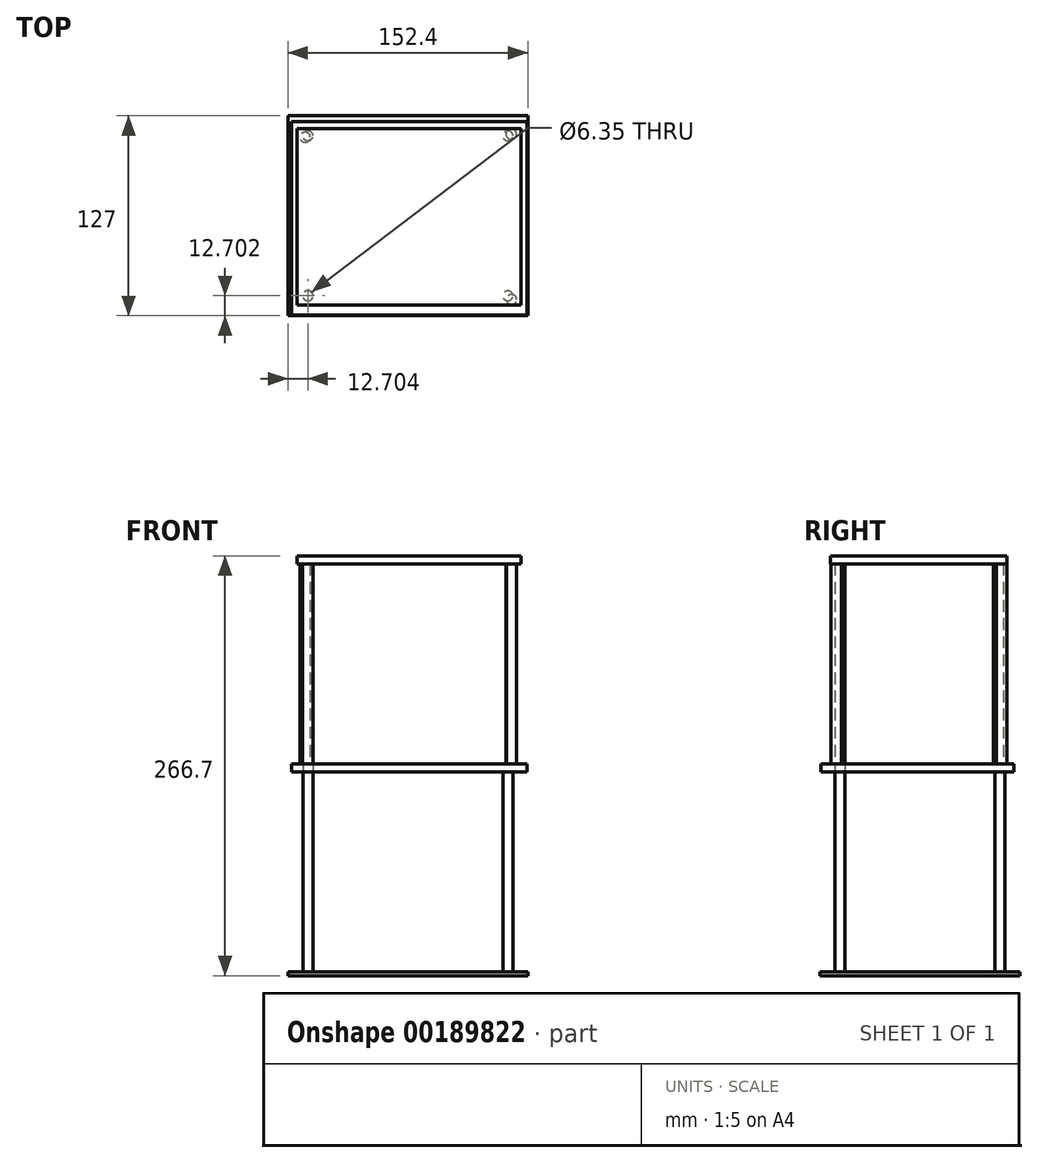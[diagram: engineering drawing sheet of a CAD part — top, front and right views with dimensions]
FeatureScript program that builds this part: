
annotation { "Feature Type Name" : "Feature", "Feature Type Description" : "" }
export const myFeature = defineFeature(function(context is Context, id is Id, definition is map)
    precondition{}
    {
        {
            var Q0;
            Q0=qCreatedBy(makeId("Top.planeOp"),FACE);
            var sketch = newSketch(context, id + "F0", { "sketchPlane" : qUnion([Q0])});
            skLineSegment(sketch, "E0.bottom", {"start": v(-67.97, -61.32) * mm, "end": v(84.43, -61.32) * mm});
            skLineSegment(sketch, "E0.top", {"start": v(-67.97, 65.68) * mm, "end": v(84.43, 65.68) * mm});
            skLineSegment(sketch, "E0.left", {"start": v(-67.97, -61.32) * mm, "end": v(-67.97, 65.68) * mm});
            skLineSegment(sketch, "E0.right", {"start": v(84.43, -61.32) * mm, "end": v(84.43, 65.68) * mm});
            skSolve(sketch);
        }
        {
            var Q0;
            Q0 = qSketchRegion(id + "F0", true);
            extrude(context, id + "F1", {"entities" : qUnion([Q0]), "oppositeDirection" : true, "depth" : 2.54 * mm});
        }
        {
            var Q0;
            Q0=makeQuery(id+"F1.opExtrude","CAP_FACE",FACE,{"disambiguationData":[OSD([sQuery(id+"F0.wireOp",EDGE,"E0.bottom"),sQuery(id+"F0.wireOp",EDGE,"E0.top"),sQuery(id+"F0.wireOp",EDGE,"E0.left"),sQuery(id+"F0.wireOp",EDGE,"E0.right")])],"isStart":true});
            var sketch = newSketch(context, id + "F2", { "sketchPlane" : qUnion([Q0])});
            skCircle(sketch, "E1", {"center": v(-55.27, -48.62) * mm, "radius": 3.18 * mm});
            skCircle(sketch, "E2", {"center": v(-55.27, 52.98) * mm, "radius": 3.18 * mm});
            skCircle(sketch, "E3", {"center": v(71.73, 52.98) * mm, "radius": 3.18 * mm});
            skCircle(sketch, "E4", {"center": v(71.73, -48.62) * mm, "radius": 3.18 * mm});
            skSolve(sketch);
        }
        {
            var Q0;
            Q0 = qSketchRegion(id + "F2", true);
            extrude(context, id + "F3", {"entities" : qUnion([Q0]), "operationType" : NewBodyOperationType.ADD, "depth" : 127 * mm});
        }
        {
            var Q0;
            Q0=makeQuery(id+"F3.opExtrude","CAP_FACE",FACE,{"disambiguationData":[OSD([sQuery(id+"F2.wireOp",EDGE,"E1")])],"isStart":false});
            var sketch = newSketch(context, id + "F4", { "sketchPlane" : qUnion([Q0])});
            skLineSegment(sketch, "E5.bottom", {"start": v(-65.76, -60.74) * mm, "end": v(83.77, -60.74) * mm});
            skLineSegment(sketch, "E5.top", {"start": v(-65.76, 61.98) * mm, "end": v(83.77, 61.98) * mm});
            skLineSegment(sketch, "E5.left", {"start": v(-65.76, -60.74) * mm, "end": v(-65.76, 61.98) * mm});
            skLineSegment(sketch, "E5.right", {"start": v(83.77, -60.74) * mm, "end": v(83.77, 61.98) * mm});
            skSolve(sketch);
        }
        {
            var Q0;
            Q0=makeQuery(id+"F4.imprint","IMPRINT",FACE,{"disambiguationData":[TD([[makeQuery(id+"F4.imprint","IMPRINT",EDGE,{"derivedFrom":sQuery(id+"F4.wireOp",EDGE,"E5.bottom")}),1.0]])]});
            extrude(context, id + "F5", {"entities" : qUnion([Q0]), "depth" : 5.08 * mm});
        }
        {
            var Q0;
            Q0=makeQuery(id+"F5.opExtrude","CAP_FACE",FACE,{"disambiguationData":[OSD([sQuery(id+"F2.wireOp",EDGE,"E1"),sQuery(id+"F4.wireOp",EDGE,"E5.bottom"),sQuery(id+"F4.wireOp",EDGE,"E5.top"),sQuery(id+"F4.wireOp",EDGE,"E5.left"),sQuery(id+"F4.wireOp",EDGE,"E5.right")])],"isStart":false});
            var sketch = newSketch(context, id + "F6", { "sketchPlane" : qUnion([Q0])});
            skCircle(sketch, "E6", {"center": v(-55.27, -48.62) * mm, "radius": 3.28 * mm});
            skCircle(sketch, "E7", {"center": v(-57, 52.07) * mm, "radius": 3.2 * mm});
            skCircle(sketch, "E8", {"center": v(73.86, 54.13) * mm, "radius": 3.34 * mm});
            skCircle(sketch, "E9", {"center": v(74.06, -51.05) * mm, "radius": 3.25 * mm});
            skSolve(sketch);
        }
        {
            var Q0;
            Q0 = qSketchRegion(id + "F6", true);
            extrude(context, id + "F7", {"entities" : qUnion([Q0]), "depth" : 127 * mm});
        }
        {
            var Q0;
            Q0=makeQuery(id+"F7.opExtrude","CAP_FACE",FACE,{"disambiguationData":[OSD([sQuery(id+"F6.wireOp",EDGE,"E6")])],"isStart":false});
            var sketch = newSketch(context, id + "F8", { "sketchPlane" : qUnion([Q0])});
            skLineSegment(sketch, "E10.bottom", {"start": v(-62.13, -54.54) * mm, "end": v(79.95, -54.54) * mm});
            skLineSegment(sketch, "E10.top", {"start": v(-62.13, 57.41) * mm, "end": v(79.95, 57.41) * mm});
            skLineSegment(sketch, "E10.left", {"start": v(-62.13, -54.54) * mm, "end": v(-62.13, 57.41) * mm});
            skLineSegment(sketch, "E10.right", {"start": v(79.95, -54.54) * mm, "end": v(79.95, 57.41) * mm});
            skSolve(sketch);
        }
        {
            var Q0;
            Q0 = qSketchRegion(id + "F8", true);
            extrude(context, id + "F9", {"entities" : qUnion([Q0]), "depth" : 5.08 * mm});
        }
    });
